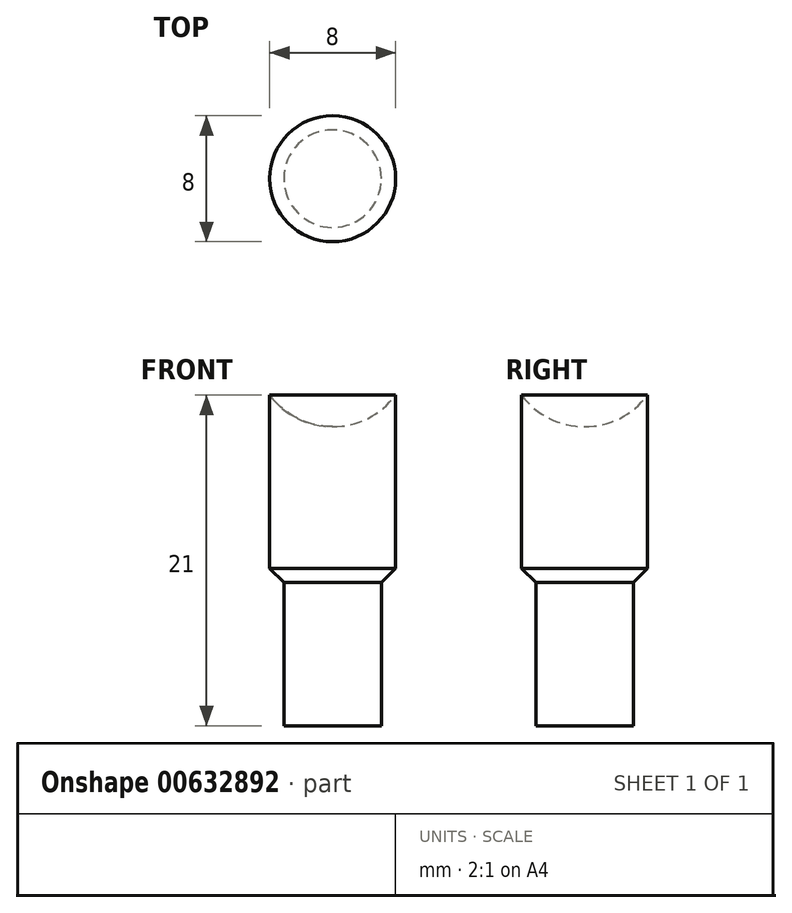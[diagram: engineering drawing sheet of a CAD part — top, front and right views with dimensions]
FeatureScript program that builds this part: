
annotation { "Feature Type Name" : "Feature", "Feature Type Description" : "" }
export const myFeature = defineFeature(function(context is Context, id is Id, definition is map)
    precondition{}
    {
        {
            var Q0;
            Q0=qCreatedBy(makeId("Front.planeOp"),FACE);
            var sketch = newSketch(context, id + "F0", { "sketchPlane" : qUnion([Q0])});
            skCircle(sketch, "E0", {"center": v(0, 15) * mm, "radius": 5 * mm});
            skLineSegment(sketch, "E1", {"start": v(-3.1, 0) * mm, "end": v(-3.1, -9) * mm});
            skLineSegment(sketch, "E2", {"start": v(-3.1, 0) * mm, "end": v(0, 0) * mm});
            skLineSegment(sketch, "E3", {"start": v(-3.1, -9) * mm, "end": v(0, -9) * mm});
            skLineSegment(sketch, "E4", {"start": v(-3.1, 0) * mm, "end": v(-4, 0) * mm});
            skLineSegment(sketch, "E5", {"start": v(-4, 0) * mm, "end": v(-4, 12) * mm});
            skLineSegment(sketch, "E6", {"start": v(-4, 12) * mm, "end": v(0, 12) * mm});
            skLineSegment(sketch, "E7", {"start": v(0, 12) * mm, "end": v(0, -9) * mm});
            skLineSegment(sketch, "E8", {"start": v(0, 12) * mm, "end": v(0, 20) * mm});
            skSolve(sketch);
        }
        {
            var Q0;
            Q0=makeQuery(id+"F0.imprint","IMPRINT",FACE,{"disambiguationData":[TD([[makeQuery(id+"F0.imprint","IMPRINT",EDGE,{"derivedFrom":sQuery(id+"F0.wireOp",EDGE,"E1")}),1.0]])]});
            var Q1;
            {var subQ1=sQuery(id+"F0.wireOp",EDGE,"E2");Q1=makeQuery(id+"F0.imprint","IMPRINT",FACE,{"disambiguationData":[TD([[makeQuery(id+"F0.imprint","IMPRINT",EDGE,{"derivedFrom":subQ1}),1.0]])]});}
            var Q2;
            Q2=sQuery(id+"F0.wireOp",EDGE,"E7");
            revolve(context, id + "F1", {"entities" : qUnion([Q0, Q1]), "axis" : qUnion([Q2]), "revolveType" : RevolveType.FULL});
        }
        {
            var Q0;
            Q0=makeQuery(id+"F1.opRevolve","SWEPT_EDGE",EDGE,{"disambiguationData":[OSD([sQuery(id+"F0.wireOp",EDGE,"E4"),sQuery(id+"F0.wireOp",EDGE,"E5")])]});
            chamfer(context, id + "F2", {"entities" : qUnion([Q0]), "width" : 1 * mm, "tangentPropagation" : true});
        }
    });
